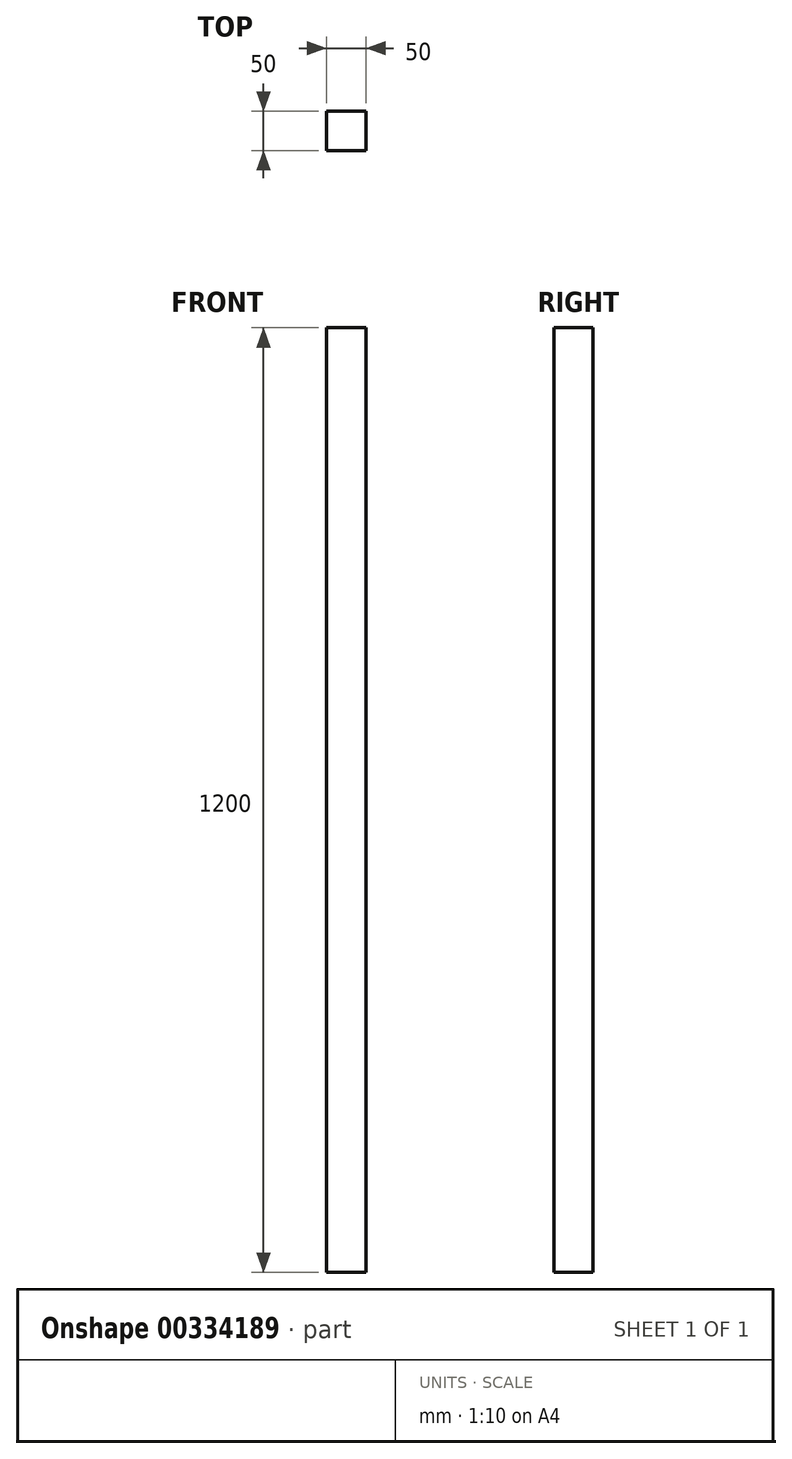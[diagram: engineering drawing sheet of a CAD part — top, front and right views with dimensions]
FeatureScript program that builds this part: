
annotation { "Feature Type Name" : "Feature", "Feature Type Description" : "" }
export const myFeature = defineFeature(function(context is Context, id is Id, definition is map)
    precondition{}
    {
        {
            var Q0;
            Q0=qCreatedBy(makeId("Front.planeOp"),FACE);
            var sketch = newSketch(context, id + "F0", { "sketchPlane" : qUnion([Q0])});
            skLineSegment(sketch, "E0.bottom", {"start": v(25, 600) * mm, "end": v(-25, 600) * mm});
            skLineSegment(sketch, "E0.top", {"start": v(25, -600) * mm, "end": v(-25, -600) * mm});
            skLineSegment(sketch, "E0.left", {"start": v(25, 600) * mm, "end": v(25, -600) * mm});
            skLineSegment(sketch, "E0.right", {"start": v(-25, 600) * mm, "end": v(-25, -600) * mm});
            skPoint(sketch, "E0.middle", {"position": v(0, 0) * mm});
            skSolve(sketch);
        }
        {
            var Q0;
            Q0 = qSketchRegion(id + "F0", true);
            extrude(context, id + "F1", {"entities" : qUnion([Q0]), "endBound" : BoundingType.SYMMETRIC, "depth" : 50 * mm});
        }
    });
